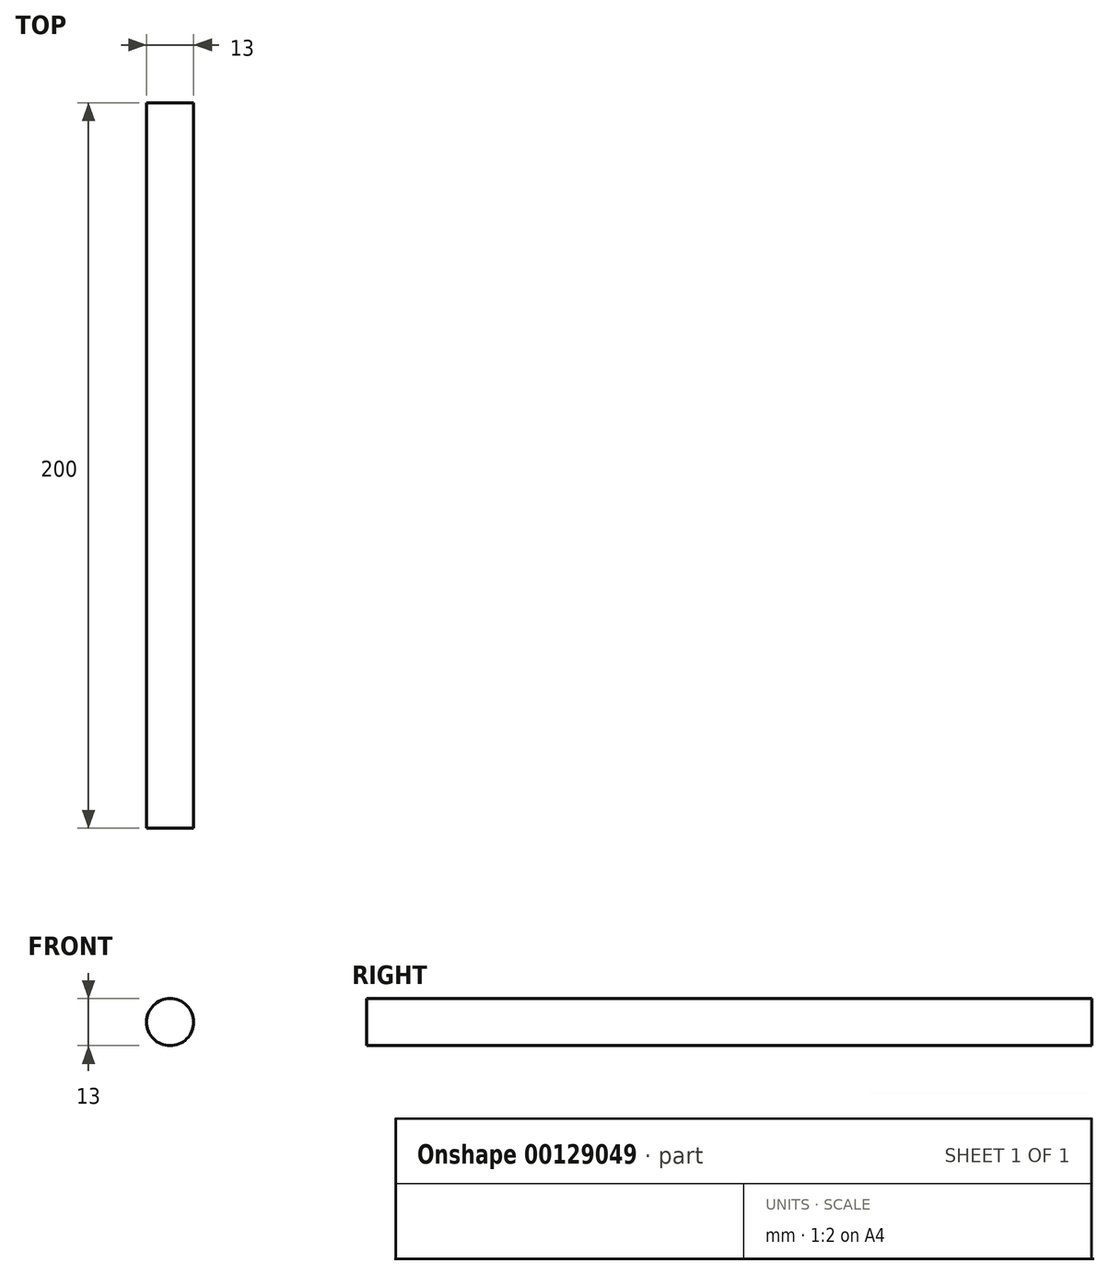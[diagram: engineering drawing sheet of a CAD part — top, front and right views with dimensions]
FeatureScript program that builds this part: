
annotation { "Feature Type Name" : "Feature", "Feature Type Description" : "" }
export const myFeature = defineFeature(function(context is Context, id is Id, definition is map)
    precondition{}
    {
        {
            var Q0;
            Q0=qCreatedBy(makeId("Front.planeOp"),FACE);
            var sketch = newSketch(context, id + "F0", { "sketchPlane" : qUnion([Q0])});
            skCircle(sketch, "E0", {"center": v(0, 0) * mm, "radius": 6.5 * mm});
            skSolve(sketch);
        }
        {
            var Q0;
            Q0=makeQuery(id+"F0.imprint","IMPRINT",FACE,{"disambiguationData":[TD([[makeQuery(id+"F0.imprint","IMPRINT",EDGE,{"derivedFrom":sQuery(id+"F0.wireOp",EDGE,"E0")}),1.0]])]});
            extrude(context, id + "F1", {"entities" : qUnion([Q0]), "depth" : 200 * mm});
        }
    });
